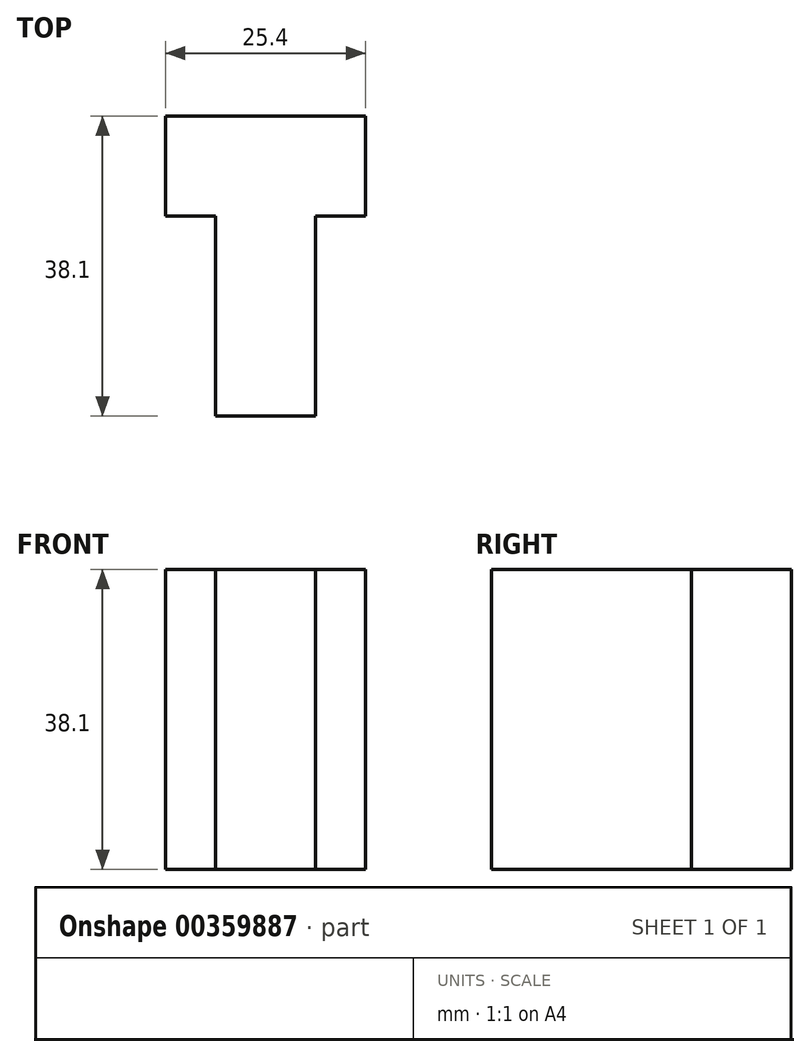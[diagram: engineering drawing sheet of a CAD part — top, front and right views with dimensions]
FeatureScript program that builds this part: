
annotation { "Feature Type Name" : "Feature", "Feature Type Description" : "" }
export const myFeature = defineFeature(function(context is Context, id is Id, definition is map)
    precondition{}
    {
        {
            var Q0;
            Q0=qCreatedBy(makeId("Top.planeOp"),FACE);
            var sketch = newSketch(context, id + "F0", { "sketchPlane" : qUnion([Q0])});
            skLineSegment(sketch, "E0", {"start": v(0, 0) * mm, "end": v(12.7, 0) * mm});
            skLineSegment(sketch, "E1", {"start": v(12.7, 0) * mm, "end": v(12.7, 25.4) * mm});
            skLineSegment(sketch, "E2", {"start": v(12.7, 25.4) * mm, "end": v(19.05, 25.4) * mm});
            skLineSegment(sketch, "E3", {"start": v(19.05, 25.4) * mm, "end": v(19.05, 38.1) * mm});
            skLineSegment(sketch, "E4", {"start": v(19.05, 38.1) * mm, "end": v(-6.35, 38.1) * mm});
            skLineSegment(sketch, "E5", {"start": v(-6.35, 38.1) * mm, "end": v(-6.35, 25.4) * mm});
            skLineSegment(sketch, "E6", {"start": v(-6.35, 25.4) * mm, "end": v(0, 25.4) * mm});
            skLineSegment(sketch, "E7", {"start": v(0, 25.4) * mm, "end": v(0, 0) * mm});
            skSolve(sketch);
        }
        {
            var Q0;
            Q0 = qSketchRegion(id + "F0", true);
            extrude(context, id + "F1", {"entities" : qUnion([Q0]), "depth" : 38.1 * mm});
        }
    });
